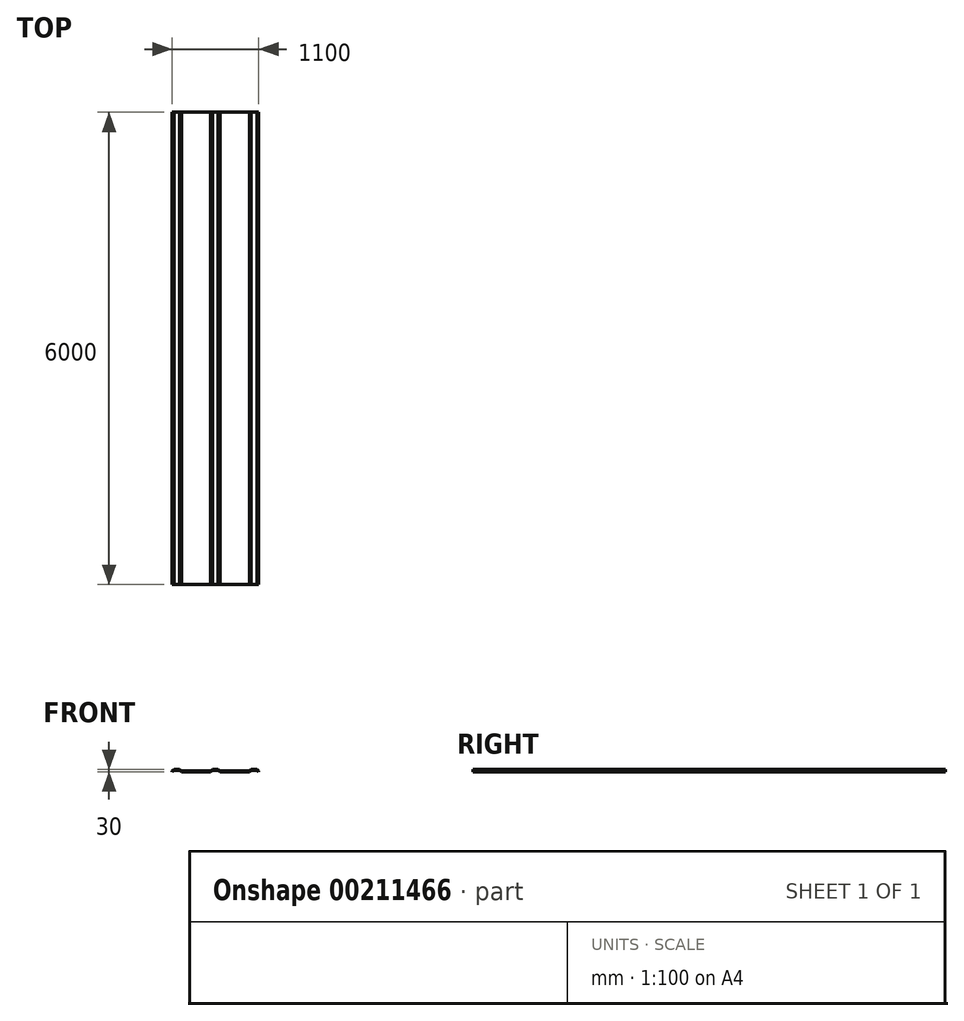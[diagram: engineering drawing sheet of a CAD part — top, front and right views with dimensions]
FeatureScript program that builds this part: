
annotation { "Feature Type Name" : "Feature", "Feature Type Description" : "" }
export const myFeature = defineFeature(function(context is Context, id is Id, definition is map)
    precondition{}
    {
        {
            var Q0;
            Q0=qCreatedBy(makeId("Front.planeOp"),FACE);
            var sketch = newSketch(context, id + "F0", { "sketchPlane" : qUnion([Q0])});
            skLineSegment(sketch, "E0", {"start": v(0, 0) * mm, "end": v(0, 0) * mm});
            skLineSegment(sketch, "E1", {"start": v(-430, 0) * mm, "end": v(-60, 0) * mm});
            skLineSegment(sketch, "E2", {"start": v(-60, 0) * mm, "end": v(-35, 20) * mm});
            skLineSegment(sketch, "E3", {"start": v(-35, 20) * mm, "end": v(35, 20) * mm});
            skLineSegment(sketch, "E4", {"start": v(35, 20) * mm, "end": v(60, 0) * mm});
            skLineSegment(sketch, "E5", {"start": v(60, 0) * mm, "end": v(430, 0) * mm});
            skLineSegment(sketch, "E6", {"start": v(430, 0) * mm, "end": v(455, 20) * mm});
            skLineSegment(sketch, "E7", {"start": v(455, 20) * mm, "end": v(525, 20) * mm});
            skLineSegment(sketch, "E8", {"start": v(525, 20) * mm, "end": v(550, 0) * mm});
            skLineSegment(sketch, "E9", {"start": v(-430, 0) * mm, "end": v(-455, 20) * mm});
            skLineSegment(sketch, "E10", {"start": v(-455, 20) * mm, "end": v(-525, 20) * mm});
            skLineSegment(sketch, "E11", {"start": v(-525, 20) * mm, "end": v(-550, 0) * mm});
            skLineSegment(sketch, "E12", {"start": v(550, 0) * mm, "end": v(550, 10) * mm});
            skLineSegment(sketch, "E13", {"start": v(550, 10) * mm, "end": v(525, 30) * mm});
            skLineSegment(sketch, "E14", {"start": v(525, 30) * mm, "end": v(455, 30) * mm});
            skLineSegment(sketch, "E15", {"start": v(455, 30) * mm, "end": v(430, 10) * mm});
            skPoint(sketch, "E15.endSnap0", {"position": v(442.5, 10) * mm});
            skLineSegment(sketch, "E16", {"start": v(430, 10) * mm, "end": v(60, 10) * mm});
            skLineSegment(sketch, "E17", {"start": v(60, 10) * mm, "end": v(35, 30) * mm});
            skLineSegment(sketch, "E18", {"start": v(35, 30) * mm, "end": v(-35, 30) * mm});
            skLineSegment(sketch, "E19", {"start": v(-35, 30) * mm, "end": v(-60, 10) * mm});
            skLineSegment(sketch, "E20", {"start": v(-60, 10) * mm, "end": v(-430, 10) * mm});
            skLineSegment(sketch, "E21", {"start": v(-430, 10) * mm, "end": v(-455, 30) * mm});
            skLineSegment(sketch, "E22", {"start": v(-455, 30) * mm, "end": v(-525, 30) * mm});
            skLineSegment(sketch, "E23", {"start": v(-525, 30) * mm, "end": v(-550, 10) * mm});
            skLineSegment(sketch, "E24", {"start": v(-550, 10) * mm, "end": v(-550, 0) * mm});
            skSolve(sketch);
        }
        {
            var Q0;
            Q0=qSketchRegion(id+"F0",true);
            extrude(context, id + "F1", {"entities" : qUnion([Q0]), "depth" : 6000 * mm, "symmetric" : true});
        }
    });
